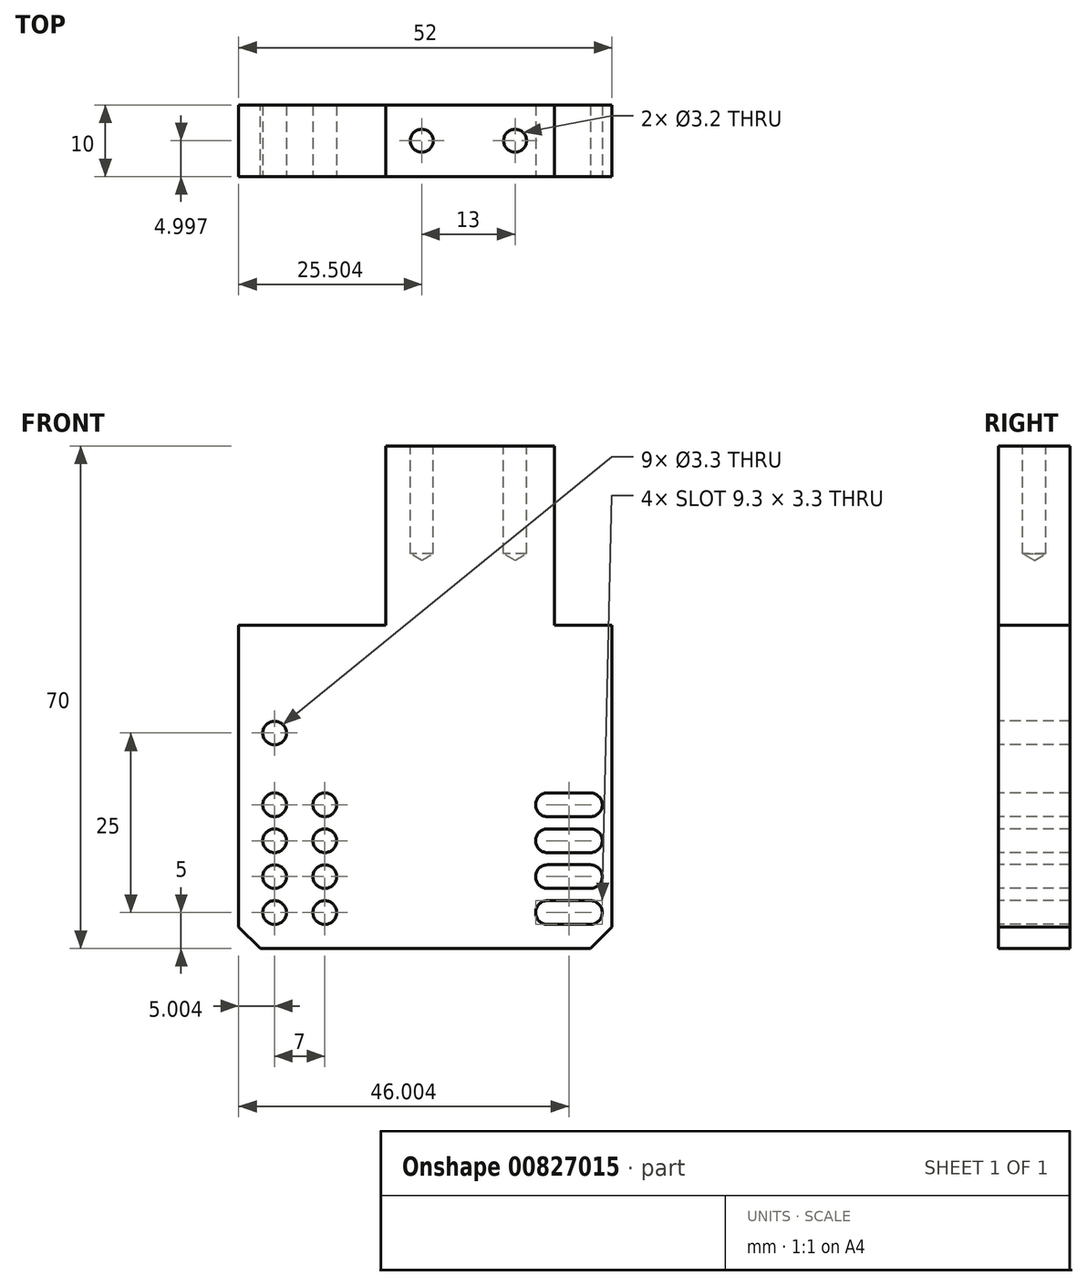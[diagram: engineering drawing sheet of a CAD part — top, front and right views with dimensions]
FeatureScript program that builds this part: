
annotation { "Feature Type Name" : "Feature", "Feature Type Description" : "" }
export const myFeature = defineFeature(function(context is Context, id is Id, definition is map)
    precondition{}
    {
        {
            var Q0;
            Q0=qCreatedBy(makeId("Top.planeOp"),FACE);
            cPlane(context, id + "F0", {"entities" : qUnion([Q0]), "cplaneType" : CPlaneType.OFFSET, "offset" : 5 * mm, "oppositeDirection" : true, "width" : 150 * mm, "height" : 150 * mm});
        }
        {
            var Q0;
            Q0=qCreatedBy(id+"F0.planeOp",FACE);
            var sketch = newSketch(context, id + "F1", { "sketchPlane" : qUnion([Q0])});
            skLineSegment(sketch, "E0.bottom", {"start": v(-161.04, 46.03) * mm, "end": v(-109.04, 46.03) * mm});
            skLineSegment(sketch, "E0.top", {"start": v(-161.04, 56.03) * mm, "end": v(-109.04, 56.03) * mm});
            skLineSegment(sketch, "E0.left", {"start": v(-161.04, 46.03) * mm, "end": v(-161.04, 56.03) * mm});
            skLineSegment(sketch, "E0.right", {"start": v(-109.04, 46.03) * mm, "end": v(-109.04, 56.03) * mm});
            skPoint(sketch, "E1", {"position": v(-135.54, 51.03) * mm});
            skPoint(sketch, "E2", {"position": v(-122.54, 51.03) * mm});
            skSolve(sketch);
        }
        {
            var Q0;
            Q0=makeQuery(id+"F1.imprint","IMPRINT",FACE,{"disambiguationData":[TD([[makeQuery(id+"F1.imprint","IMPRINT",EDGE,{"derivedFrom":sQuery(id+"F1.wireOp",EDGE,"E0.bottom")}),1.0]])]});
            extrude(context, id + "F2", {"entities" : qUnion([Q0]), "oppositeDirection" : true, "depth" : 70 * mm, "offsetDistance" : 25 * mm});
        }
        {
            var Q0;
            Q0=sQuery(id+"F1.wireOp",VERTEX,"E1");
            var Q1;
            Q1=sQuery(id+"F1.wireOp",VERTEX,"E2");
            var Q2;
            Q2=makeQuery(id+"F2.opExtrude","SWEPT_BODY",BODY,{"disambiguationData":[OSD([sQuery(id+"F1.wireOp",EDGE,"E0.bottom"),sQuery(id+"F1.wireOp",EDGE,"E0.top"),sQuery(id+"F1.wireOp",EDGE,"E0.left"),sQuery(id+"F1.wireOp",EDGE,"E0.right")])]});
            hole(context, id + "F3", {"style" : HoleStyle.SIMPLE, "endStyle" : HoleEndStyle.BLIND, "holeDiameter" : 3.2 * mm, "majorDiameter" : 5 * mm, "holeDepth" : 15 * mm, "isTappedThrough" : true, "tappedDepth" : 12 * mm, "tapClearance" : 3, "startFromSketch" : true, "locations" : qUnion([Q0, Q1]), "scope" : qUnion([Q2])});
        }
        {
            var Q0;
            Q0=makeQuery(id+"F2.opExtrude","SWEPT_FACE",FACE,{"disambiguationData":[OSD([sQuery(id+"F1.wireOp",EDGE,"E0.bottom")])]});
            var sketch = newSketch(context, id + "F4", { "sketchPlane" : qUnion([Q0])});
            skLineSegment(sketch, "E3", {"start": v(-161.04, -15) * mm, "end": v(-109.04, -15) * mm, "construction": true});
            skLineSegment(sketch, "E4", {"start": v(-156.04, -15) * mm, "end": v(-156.04, -75) * mm, "construction": true});
            skLineSegment(sketch, "E5.1.4.4", {"start": v(-121.04, 25) * mm, "end": v(-121.04, -35) * mm, "construction": true});
            skPoint(sketch, "E6", {"position": v(-156.04, -70) * mm});
            skPoint(sketch, "E7.0.1.0", {"position": v(-156.04, -60) * mm});
            skPoint(sketch, "E7.0.4.0", {"position": v(-156.04, -55) * mm});
            skLineSegment(sketch, "E7.direction2", {"start": v(-156.04, -70) * mm, "end": v(-156.04, -60) * mm, "construction": true});
            skArc(sketch, "E8", {"start": v(-118.04, -68.35) * mm, "mid": v(-119.69, -70) * mm, "end": v(-118.04, -71.65) * mm});
            skArc(sketch, "E9", {"start": v(-112.04, -71.65) * mm, "mid": v(-110.39, -70) * mm, "end": v(-112.04, -68.35) * mm});
            skLineSegment(sketch, "E10", {"start": v(-112.04, -71.65) * mm, "end": v(-118.04, -71.65) * mm});
            skLineSegment(sketch, "E11", {"start": v(-118.04, -68.35) * mm, "end": v(-112.04, -68.35) * mm});
            skArc(sketch, "E12.0.1.0", {"start": v(-118.04, -63.35) * mm, "mid": v(-119.69, -65) * mm, "end": v(-118.04, -66.65) * mm});
            skArc(sketch, "E12.0.1.1", {"start": v(-112.04, -66.65) * mm, "mid": v(-110.39, -65) * mm, "end": v(-112.04, -63.35) * mm});
            skLineSegment(sketch, "E12.0.1.2", {"start": v(-112.04, -66.65) * mm, "end": v(-118.04, -66.65) * mm});
            skLineSegment(sketch, "E12.0.1.3", {"start": v(-118.04, -63.35) * mm, "end": v(-112.04, -63.35) * mm});
            skArc(sketch, "E12.0.2.0", {"start": v(-118.04, -58.35) * mm, "mid": v(-119.69, -60) * mm, "end": v(-118.04, -61.65) * mm});
            skArc(sketch, "E12.0.2.1", {"start": v(-112.04, -61.65) * mm, "mid": v(-110.39, -60) * mm, "end": v(-112.04, -58.35) * mm});
            skLineSegment(sketch, "E12.0.2.2", {"start": v(-112.04, -61.65) * mm, "end": v(-118.04, -61.65) * mm});
            skLineSegment(sketch, "E12.0.2.3", {"start": v(-118.04, -58.35) * mm, "end": v(-112.04, -58.35) * mm});
            skLineSegment(sketch, "E12.direction1", {"start": v(-118.04, -71.65) * mm, "end": v(-91.04, -71.65) * mm, "construction": true});
            skLineSegment(sketch, "E12.direction2", {"start": v(-118.04, -71.65) * mm, "end": v(-118.04, -66.65) * mm, "construction": true});
            skPoint(sketch, "E13", {"position": v(-156.04, -65) * mm});
            skArc(sketch, "E14.0.0.3", {"start": v(-118.04, -53.35) * mm, "mid": v(-119.69, -55) * mm, "end": v(-118.04, -56.65) * mm});
            skArc(sketch, "E14.4.0.3", {"start": v(-112.04, -56.65) * mm, "mid": v(-110.39, -55) * mm, "end": v(-112.04, -53.35) * mm});
            skLineSegment(sketch, "E14.8.0.3", {"start": v(-112.04, -56.65) * mm, "end": v(-118.04, -56.65) * mm});
            skLineSegment(sketch, "E14.11.0.3", {"start": v(-118.04, -53.35) * mm, "end": v(-112.04, -53.35) * mm});
            skPoint(sketch, "E15", {"position": v(-156.04, -45) * mm});
            skPoint(sketch, "E16", {"position": v(-149.04, -70) * mm});
            skPoint(sketch, "E17.0.1.0", {"position": v(-149.04, -65) * mm});
            skPoint(sketch, "E17.0.2.0", {"position": v(-149.04, -60) * mm});
            skPoint(sketch, "E17.0.3.0", {"position": v(-149.04, -55) * mm});
            skLineSegment(sketch, "E17.direction1", {"start": v(-149.04, -70) * mm, "end": v(-126.04, -70) * mm, "construction": true});
            skLineSegment(sketch, "E17.direction2", {"start": v(-149.04, -70) * mm, "end": v(-149.04, -65) * mm, "construction": true});
            skSolve(sketch);
        }
        {
            var Q0;
            Q0=sQuery(id+"F4.wireOp",VERTEX,"E6");
            var Q1;
            Q1=sQuery(id+"F4.wireOp",VERTEX,"E7.0.1.0");
            var Q2;
            Q2=sQuery(id+"F4.wireOp",VERTEX,"E7.0.2.0");
            var Q3;
            Q3=sQuery(id+"F4.wireOp",VERTEX,"E7.0.3.0");
            var Q4;
            Q4=sQuery(id+"F4.wireOp",VERTEX,"E7.0.4.0");
            var Q5;
            Q5=sQuery(id+"F4.wireOp",VERTEX,"E13");
            var Q6;
            Q6=sQuery(id+"F4.wireOp",VERTEX,"E15");
            var Q7;
            Q7=sQuery(id+"F4.wireOp",VERTEX,"E16");
            var Q8;
            Q8=sQuery(id+"F4.wireOp",VERTEX,"E17.direction2.end");
            var Q9;
            Q9=sQuery(id+"F4.wireOp",VERTEX,"E17.0.2.0");
            var Q10;
            Q10=sQuery(id+"F4.wireOp",VERTEX,"E17.0.3.0");
            var Q11;
            Q11=makeQuery(id+"F2.opExtrude","SWEPT_BODY",BODY,{"disambiguationData":[OSD([sQuery(id+"F1.wireOp",EDGE,"E0.bottom"),sQuery(id+"F1.wireOp",EDGE,"E0.top"),sQuery(id+"F1.wireOp",EDGE,"E0.left"),sQuery(id+"F1.wireOp",EDGE,"E0.right")])]});
            hole(context, id + "F5", {"style" : HoleStyle.SIMPLE, "endStyle" : HoleEndStyle.THROUGH, "standardTappedOrClearance" : lookupTablePath({ "fit" : "Normal", "standard" : "ISO", "size" : "M3", "type" : "Clearance" }), "standardBlindInLast" : lookupTablePath({ "fit" : "Standard", "standard" : "ISO", "size" : "M3", "type" : "Clearance" }), "holeDiameter" : 3.3 * mm, "majorDiameter" : 5 * mm, "isTappedThrough" : true, "tappedDepth" : 12 * mm, "tapClearance" : 3, "startFromSketch" : true, "locations" : qUnion([Q0, Q1, Q2, Q3, Q4, Q5, Q6, Q7, Q8, Q9, Q10]), "scope" : qUnion([Q11])});
        }
        {
            var Q0;
            Q0=makeQuery(id+"F4.imprint","IMPRINT",FACE,{"disambiguationData":[TD([[makeQuery(id+"F4.imprint","IMPRINT",EDGE,{"derivedFrom":sQuery(id+"F4.wireOp",EDGE,"E8")}),1.0]])]});
            var Q1;
            Q1=makeQuery(id+"F4.imprint","IMPRINT",FACE,{"disambiguationData":[TD([[makeQuery(id+"F4.imprint","IMPRINT",EDGE,{"derivedFrom":sQuery(id+"F4.wireOp",EDGE,"E12.0.1.0")}),1.0]])]});
            var Q2;
            Q2=makeQuery(id+"F4.imprint","IMPRINT",FACE,{"disambiguationData":[TD([[makeQuery(id+"F4.imprint","IMPRINT",EDGE,{"derivedFrom":sQuery(id+"F4.wireOp",EDGE,"E12.0.2.0")}),1.0]])]});
            var Q3;
            Q3=makeQuery(id+"F4.imprint","IMPRINT",FACE,{"disambiguationData":[TD([[makeQuery(id+"F4.imprint","IMPRINT",EDGE,{"derivedFrom":sQuery(id+"F4.wireOp",EDGE,"E14.0.0.3")}),1.0]])]});
            extrude(context, id + "F6", {"entities" : qUnion([Q0, Q1, Q2, Q3]), "operationType" : NewBodyOperationType.REMOVE, "oppositeDirection" : true, "depth" : 25 * mm, "offsetDistance" : 25 * mm});
        }
        {
            var Q0;
            Q0=qCreatedBy(id+"F0.planeOp",FACE);
            var sketch = newSketch(context, id + "F7", { "sketchPlane" : qUnion([Q0])});
            skLineSegment(sketch, "E18.bottom", {"start": v(-117.04, 46.03) * mm, "end": v(-109.04, 46.03) * mm});
            skLineSegment(sketch, "E18.top", {"start": v(-117.04, 56.03) * mm, "end": v(-109.04, 56.03) * mm});
            skLineSegment(sketch, "E18.left", {"start": v(-117.04, 46.03) * mm, "end": v(-117.04, 56.03) * mm});
            skLineSegment(sketch, "E18.right", {"start": v(-109.04, 46.03) * mm, "end": v(-109.04, 56.03) * mm});
            skLineSegment(sketch, "E19.bottom", {"start": v(-161.04, 46.03) * mm, "end": v(-140.54, 46.03) * mm});
            skLineSegment(sketch, "E19.top", {"start": v(-161.04, 56.03) * mm, "end": v(-140.54, 56.03) * mm});
            skLineSegment(sketch, "E19.left", {"start": v(-161.04, 46.03) * mm, "end": v(-161.04, 56.03) * mm});
            skLineSegment(sketch, "E19.right", {"start": v(-140.54, 46.03) * mm, "end": v(-140.54, 56.03) * mm});
            skSolve(sketch);
        }
        {
            var Q0;
            Q0 = qSketchRegion(id + "F7", true);
            extrude(context, id + "F8", {"entities" : qUnion([Q0]), "operationType" : NewBodyOperationType.REMOVE, "oppositeDirection" : true, "depth" : 25 * mm, "offsetDistance" : 25 * mm});
        }
        {
            var Q0;
            Q0=makeQuery(id+"F8.boolean.opBoolean","COPY",EDGE,{"derivedFrom":makeQuery(id+"F8.opExtrude","CAP_EDGE",EDGE,{"disambiguationData":[OSD([sQuery(id+"F7.wireOp",EDGE,"E19.left")])],"isStart":false})});
            var Q1;
            Q1=makeQuery(id+"F8.boolean.opBoolean","COPY",EDGE,{"derivedFrom":makeQuery(id+"F8.opExtrude","CAP_EDGE",EDGE,{"disambiguationData":[OSD([sQuery(id+"F7.wireOp",EDGE,"E18.right")])],"isStart":false})});
            var Q2;
            Q2=makeQuery(id+"F2.opExtrude","CAP_EDGE",EDGE,{"disambiguationData":[OSD([sQuery(id+"F1.wireOp",EDGE,"E0.left")])],"isStart":false});
            var Q3;
            Q3=makeQuery(id+"F2.opExtrude","CAP_EDGE",EDGE,{"disambiguationData":[OSD([sQuery(id+"F1.wireOp",EDGE,"E0.right")])],"isStart":false});
            chamfer(context, id + "F9", {"entities" : qUnion([Q0, Q1, Q2, Q3]), "width" : 3 * mm, "tangentPropagation" : true});
        }
    });
